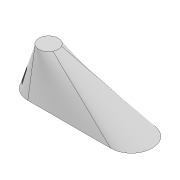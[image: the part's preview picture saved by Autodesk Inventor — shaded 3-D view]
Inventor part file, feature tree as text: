
AUTODESK INVENTOR PART (.ipt)
format: ipt  version: 2022 (Build 260153000, 153)  size: 436,736 bytes
history: native  units: mm
features: sketch x8, extrude x5, plane x2, loft x2, fillet x2, shell x1, projected_geometry x1
ambient origin geometry x8: Origin, YZ Plane, XZ Plane, XY Plane, X Axis, Y Axis, Z Axis, Center Point
bodies: Solid1 (feature_tree)
feature tree (21):
  sketch  "Sketch1"  dims[d0=14.0mm d3=-28.0mm d4=30.0mm]
  plane  "Work Plane3"
  loft  "Loft1"
  shell  "Shell1"  Thickness=30.0mm
  extrude  "Extrusion11"  TaperAngle=0.0deg  [1 undecoded]
  sketch  "Sketch9"  dims[d8=0.0mm d9=90.0deg d10=3.5mm]
  extrude  "Extrusion6"  Depth=3.5mm
  extrude  "Extrusion7"  Depth=10.0mm TaperAngle=0.0deg
  sketch  "Sketch10"  dims[d53=5.0mm d54=10.0mm d55=0.0mm]
  plane  "Work Plane4"
  loft  "Loft2"
  extrude  "Extrusion8"  Depth=9.0mm
  fillet  "Fillet1"  [1 undecoded]
  fillet  "Fillet2"  [1 undecoded]
  extrude  "Extrusion10"  Depth=30.0mm TaperAngle=0.0deg
  sketch  "Sketch3"  dims[d5=60.0mm d6=0.0mm d7=90.0deg]
  projected_geometry  "Projected Loop2"
  sketch  "Sketch11"  dims[d56=5.0mm d57=0.0mm d58=10.2mm]
  sketch  "Sketch12"  dims[d59=25.0mm d60=9.0mm d61=0.0mm d62=90.0deg d63=0.0mm d64=90.0deg]
  sketch  "Sketch15"  dims[d65=5.0mm d66=30.0mm d67=0.0mm]
  sketch  "Sketch16"  dims[d68=2.0mm d69=2.0mm d72=40.0mm d74=6.0mm d75=10.0mm d77=10.0mm d79=5.0mm d80=0.0mm d81=4.0mm d82=8.0mm d83=1.5mm d84=8.0mm d85=100.0mm d86=0.0mm]
note: 3 required parameter values undecoded (feature->parameter linkage not recoverable at this tier; creation-order binding heuristic only, values carry confidence <= 0.55)
